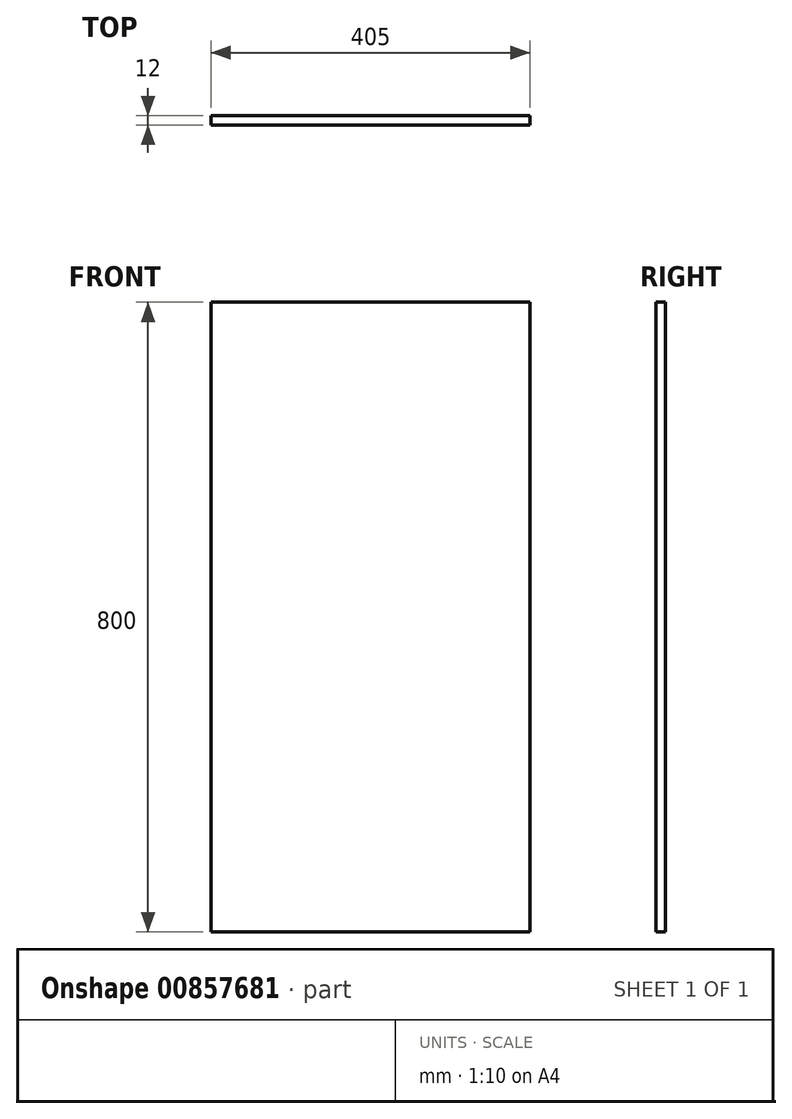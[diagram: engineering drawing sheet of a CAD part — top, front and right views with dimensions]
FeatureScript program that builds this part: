
annotation { "Feature Type Name" : "Feature", "Feature Type Description" : "" }
export const myFeature = defineFeature(function(context is Context, id is Id, definition is map)
    precondition{}
    {
        {
            var Q0;
            Q0=qCreatedBy(makeId("Front.planeOp"),FACE);
            var sketch = newSketch(context, id + "F0", { "sketchPlane" : qUnion([Q0])});
            skLineSegment(sketch, "E0.bottom", {"start": v(202.5, -400) * mm, "end": v(-202.5, -400) * mm});
            skLineSegment(sketch, "E0.top", {"start": v(202.5, 400) * mm, "end": v(-202.5, 400) * mm});
            skLineSegment(sketch, "E0.left", {"start": v(202.5, -400) * mm, "end": v(202.5, 400) * mm});
            skLineSegment(sketch, "E0.right", {"start": v(-202.5, -400) * mm, "end": v(-202.5, 400) * mm});
            skPoint(sketch, "E0.middle", {"position": v(0, 0) * mm});
            skSolve(sketch);
        }
        {
            var Q0;
            Q0=makeQuery(id+"F0.imprint","IMPRINT",FACE,{"disambiguationData":[TD([[makeQuery(id+"F0.imprint","IMPRINT",EDGE,{"derivedFrom":sQuery(id+"F0.wireOp",EDGE,"E0.bottom")}),-1.0]])]});
            extrude(context, id + "F1", {"entities" : qUnion([Q0]), "depth" : 12 * mm, "offsetDistance" : 25 * mm});
        }
    });
